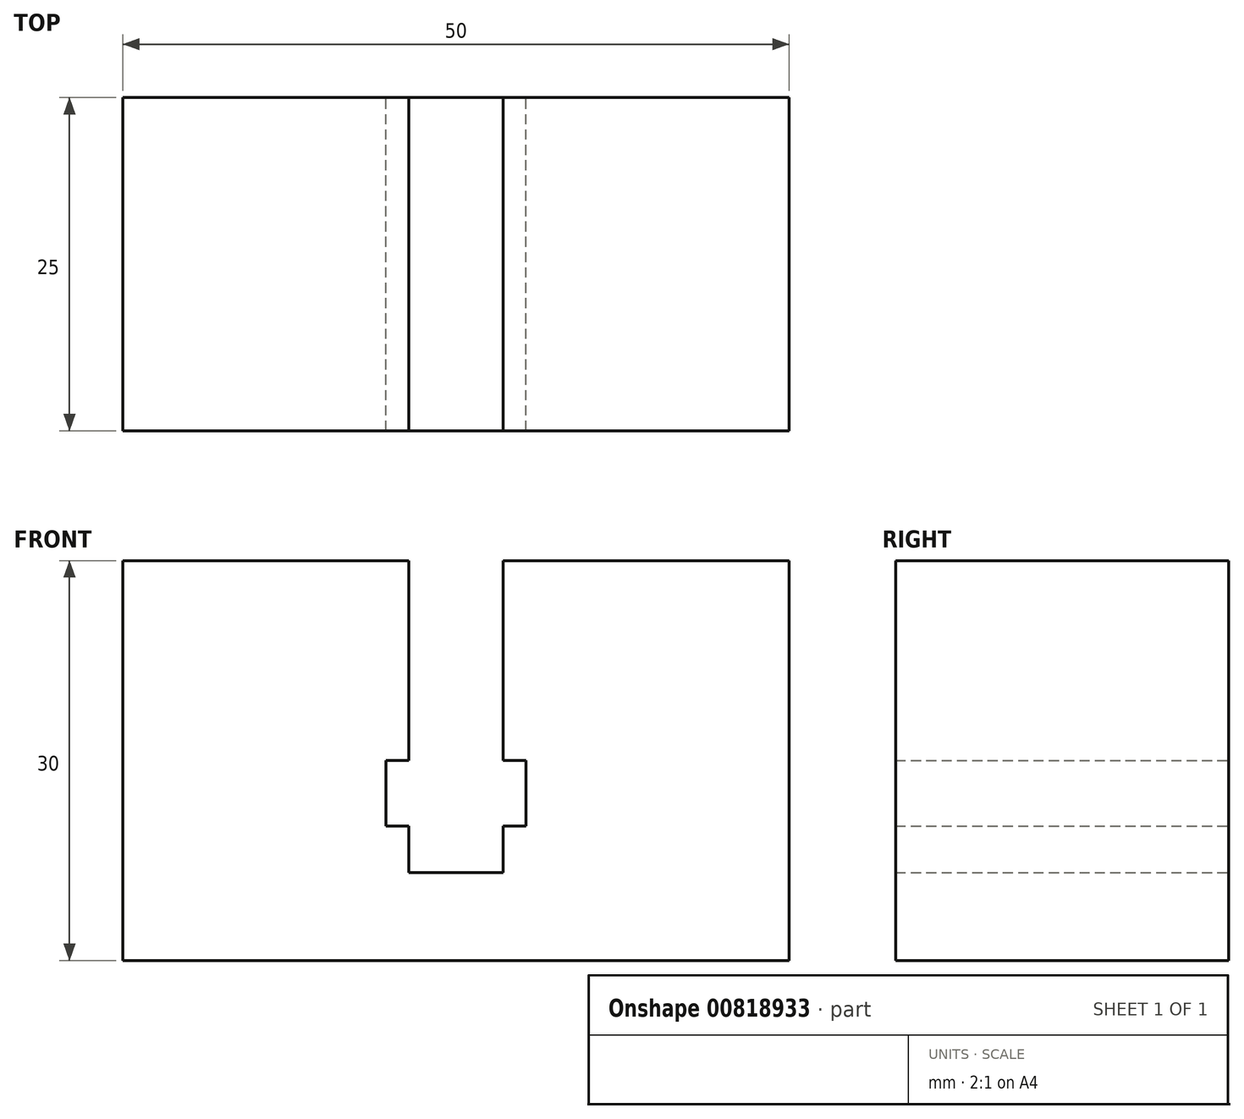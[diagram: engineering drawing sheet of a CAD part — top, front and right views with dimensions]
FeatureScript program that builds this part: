
annotation { "Feature Type Name" : "Feature", "Feature Type Description" : "" }
export const myFeature = defineFeature(function(context is Context, id is Id, definition is map)
    precondition{}
    {
        {
            var Q0;
            Q0=qCreatedBy(makeId("Front.planeOp"),FACE);
            var sketch = newSketch(context, id + "F0", { "sketchPlane" : qUnion([Q0])});
            skLineSegment(sketch, "E0.bottom", {"start": v(25, -15) * mm, "end": v(-25, -15) * mm});
            skLineSegment(sketch, "E0.top", {"start": v(25, 15) * mm, "end": v(3.55, 15) * mm});
            skLineSegment(sketch, "E0.left", {"start": v(25, -15) * mm, "end": v(25, 15) * mm});
            skLineSegment(sketch, "E0.right", {"start": v(-25, -15) * mm, "end": v(-25, 15) * mm});
            skPoint(sketch, "E0.middle", {"position": v(0, 0) * mm});
            skLineSegment(sketch, "E1.bottom", {"start": v(5.25, 0) * mm, "end": v(3.55, 0) * mm});
            skLineSegment(sketch, "E1.top", {"start": v(5.25, -4.9) * mm, "end": v(3.55, -4.9) * mm});
            skLineSegment(sketch, "E1.left", {"start": v(5.25, 0) * mm, "end": v(5.25, -4.9) * mm});
            skLineSegment(sketch, "E1.right", {"start": v(-5.25, 0) * mm, "end": v(-5.25, -4.9) * mm});
            skPoint(sketch, "E1.middle", {"position": v(0, -2.45) * mm});
            skLineSegment(sketch, "E2.left", {"start": v(3.55, -8.42) * mm, "end": v(3.55, -4.9) * mm});
            skLineSegment(sketch, "E2.right", {"start": v(-3.55, -8.42) * mm, "end": v(-3.55, -4.9) * mm});
            skPoint(sketch, "E2.middle", {"position": v(0, 7.98) * mm});
            skPoint(sketch, "E2.top.end.orphan", {"position": v(-3.55, 17.22) * mm});
            skPoint(sketch, "E3.orphan", {"position": v(3.55, 24.38) * mm});
            skLineSegment(sketch, "E4.trimOffspring", {"start": v(-3.55, 15) * mm, "end": v(-25, 15) * mm});
            skPoint(sketch, "E5.orphan", {"position": v(-3.55, -8.42) * mm});
            skLineSegment(sketch, "E6.trimOffspring", {"start": v(-3.55, 0) * mm, "end": v(-5.25, 0) * mm});
            skPoint(sketch, "E7.orphan", {"position": v(3.55, -1.26) * mm});
            skLineSegment(sketch, "E8", {"start": v(-3.55, -8.42) * mm, "end": v(3.55, -8.42) * mm});
            skLineSegment(sketch, "E9.trimOffspring", {"start": v(-3.55, -4.9) * mm, "end": v(-5.25, -4.9) * mm});
            skLineSegment(sketch, "E10.trimOffspring", {"start": v(3.55, 0) * mm, "end": v(3.55, 15) * mm});
            skLineSegment(sketch, "E11.trimOffspring", {"start": v(-3.55, 0) * mm, "end": v(-3.55, 15) * mm});
            skSolve(sketch);
        }
        {
            var Q0;
            Q0=makeQuery(id+"F0.imprint","IMPRINT",FACE,{"disambiguationData":[TD([[makeQuery(id+"F0.imprint","IMPRINT",EDGE,{"derivedFrom":sQuery(id+"F0.wireOp",EDGE,"E0.bottom")}),-1.0]])]});
            extrude(context, id + "F1", {"entities" : qUnion([Q0]), "depth" : 25 * mm, "offsetDistance" : 25 * mm});
        }
    });
